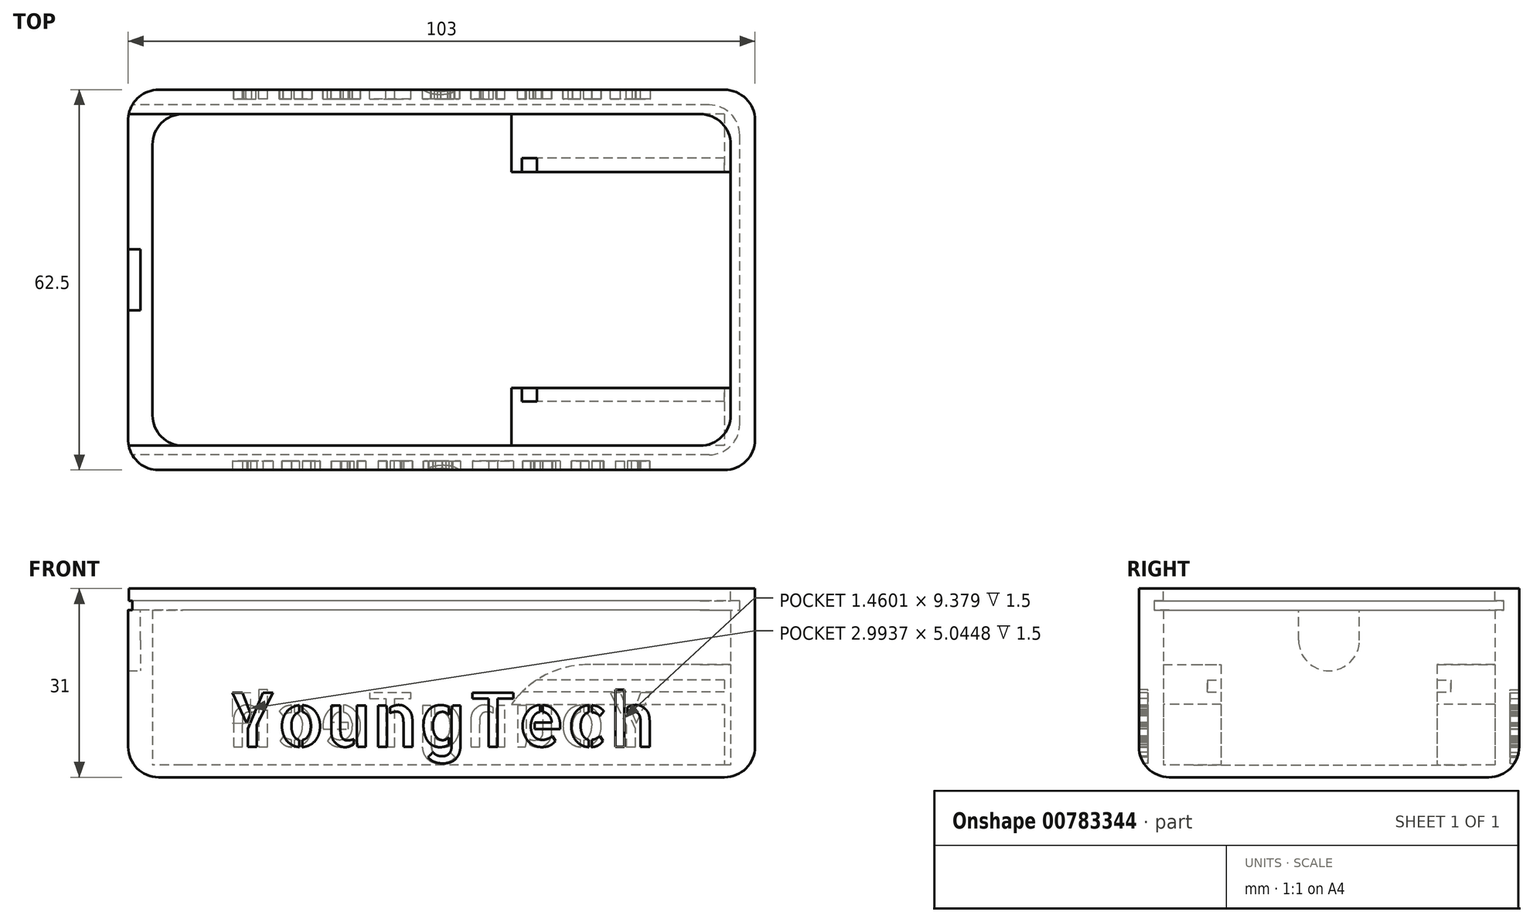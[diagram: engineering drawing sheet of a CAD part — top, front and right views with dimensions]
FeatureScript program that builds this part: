
annotation { "Feature Type Name" : "Feature", "Feature Type Description" : "" }
export const myFeature = defineFeature(function(context is Context, id is Id, definition is map)
    precondition{}
    {
        {
            var Q0;
            Q0=qCreatedBy(makeId("Top.planeOp"),FACE);
            var sketch = newSketch(context, id + "F0", { "sketchPlane" : qUnion([Q0])});
            skLineSegment(sketch, "E0.bottom", {"start": v(51.5, -31.25) * mm, "end": v(-51.5, -31.25) * mm});
            skLineSegment(sketch, "E0.top", {"start": v(51.5, 31.25) * mm, "end": v(-51.5, 31.25) * mm});
            skLineSegment(sketch, "E0.left", {"start": v(51.5, -31.25) * mm, "end": v(51.5, 31.25) * mm});
            skLineSegment(sketch, "E0.right", {"start": v(-51.5, -31.25) * mm, "end": v(-51.5, 31.25) * mm});
            skPoint(sketch, "E0.middle", {"position": v(0, 0) * mm});
            skSolve(sketch);
        }
        {
            var Q0;
            Q0=qSketchRegion(id+"F0",true);
            extrude(context, id + "F1", {"entities" : qUnion([Q0]), "depth" : 2 * mm, "offsetDistance" : 25 * mm});
        }
        {
            var Q0;
            Q0=makeQuery(id+"F1.opExtrude","CAP_FACE",FACE,{"disambiguationData":[OSD([sQuery(id+"F0.wireOp",EDGE,"E0.bottom"),sQuery(id+"F0.wireOp",EDGE,"E0.top"),sQuery(id+"F0.wireOp",EDGE,"E0.left"),sQuery(id+"F0.wireOp",EDGE,"E0.right")])],"isStart":false});
            var sketch = newSketch(context, id + "F2", { "sketchPlane" : qUnion([Q0])});
            skLineSegment(sketch, "E1.0.0", {"start": v(51.5, 31.25) * mm, "end": v(51.5, -31.25) * mm});
            skLineSegment(sketch, "E1.0.1", {"start": v(51.5, -31.25) * mm, "end": v(-51.5, -31.25) * mm});
            skLineSegment(sketch, "E1.0.2", {"start": v(-51.5, -31.25) * mm, "end": v(-51.5, 31.25) * mm});
            skLineSegment(sketch, "E1.0.3", {"start": v(-51.5, 31.25) * mm, "end": v(51.5, 31.25) * mm});
            skLineSegment(sketch, "E2.bottom", {"start": v(47.5, -27.25) * mm, "end": v(-47.5, -27.25) * mm});
            skLineSegment(sketch, "E2.top", {"start": v(47.5, 27.25) * mm, "end": v(-47.5, 27.25) * mm});
            skLineSegment(sketch, "E2.left", {"start": v(47.5, -27.25) * mm, "end": v(47.5, 27.25) * mm});
            skLineSegment(sketch, "E2.right", {"start": v(-47.5, -27.25) * mm, "end": v(-47.5, 27.25) * mm});
            skPoint(sketch, "E2.middle", {"position": v(0, 0) * mm});
            skSolve(sketch);
        }
        {
            var Q0;
            Q0=makeQuery(id+"F2.imprint","IMPRINT",FACE,{"disambiguationData":[TD([[makeQuery(id+"F2.imprint","IMPRINT",EDGE,{"derivedFrom":sQuery(id+"F2.wireOp",EDGE,"E1.0.0")}),1.0]])]});
            extrude(context, id + "F3", {"entities" : qUnion([Q0]), "operationType" : NewBodyOperationType.ADD, "depth" : 29 * mm, "offsetDistance" : 25 * mm});
        }
        {
            var Q0;
            Q0=makeQuery(id+"F3.boolean.opBoolean","MERGE",EDGE,{"derivedFrom":[makeQuery(id+"F1.opExtrude","SWEPT_EDGE",EDGE,{"disambiguationData":[OSD([sQuery(id+"F0.wireOp",EDGE,"E0.top"),sQuery(id+"F0.wireOp",EDGE,"E0.right")])]}),makeQuery(id+"F3.opExtrude","SWEPT_EDGE",EDGE,{"disambiguationData":[OSD([sQuery(id+"F2.wireOp",EDGE,"E1.0.2"),sQuery(id+"F2.wireOp",EDGE,"E1.0.3")])]})]});
            var Q1;
            Q1=makeQuery(id+"F3.boolean.opBoolean","MERGE",EDGE,{"derivedFrom":[makeQuery(id+"F1.opExtrude","SWEPT_EDGE",EDGE,{"disambiguationData":[OSD([sQuery(id+"F0.wireOp",EDGE,"E0.bottom"),sQuery(id+"F0.wireOp",EDGE,"E0.right")])]}),makeQuery(id+"F3.opExtrude","SWEPT_EDGE",EDGE,{"disambiguationData":[OSD([sQuery(id+"F2.wireOp",EDGE,"E1.0.1"),sQuery(id+"F2.wireOp",EDGE,"E1.0.2")])]})]});
            var Q2;
            Q2=makeQuery(id+"F3.boolean.opBoolean","MERGE",EDGE,{"derivedFrom":[makeQuery(id+"F1.opExtrude","SWEPT_EDGE",EDGE,{"disambiguationData":[OSD([sQuery(id+"F0.wireOp",EDGE,"E0.bottom"),sQuery(id+"F0.wireOp",EDGE,"E0.left")])]}),makeQuery(id+"F3.opExtrude","SWEPT_EDGE",EDGE,{"disambiguationData":[OSD([sQuery(id+"F2.wireOp",EDGE,"E1.0.0"),sQuery(id+"F2.wireOp",EDGE,"E1.0.1")])]})]});
            var Q3;
            Q3=makeQuery(id+"F3.opExtrude","SWEPT_EDGE",EDGE,{"disambiguationData":[OSD([sQuery(id+"F2.wireOp",EDGE,"E2.top"),sQuery(id+"F2.wireOp",EDGE,"E2.left")])]});
            var Q4;
            Q4=makeQuery(id+"F3.boolean.opBoolean","MERGE",EDGE,{"derivedFrom":[makeQuery(id+"F1.opExtrude","SWEPT_EDGE",EDGE,{"disambiguationData":[OSD([sQuery(id+"F0.wireOp",EDGE,"E0.top"),sQuery(id+"F0.wireOp",EDGE,"E0.left")])]}),makeQuery(id+"F3.opExtrude","SWEPT_EDGE",EDGE,{"disambiguationData":[OSD([sQuery(id+"F2.wireOp",EDGE,"E1.0.0"),sQuery(id+"F2.wireOp",EDGE,"E1.0.3")])]})]});
            var Q5;
            Q5=makeQuery(id+"F3.opExtrude","SWEPT_EDGE",EDGE,{"disambiguationData":[OSD([sQuery(id+"F2.wireOp",EDGE,"E2.top"),sQuery(id+"F2.wireOp",EDGE,"E2.right")])]});
            var Q6;
            Q6=makeQuery(id+"F3.opExtrude","SWEPT_EDGE",EDGE,{"disambiguationData":[OSD([sQuery(id+"F2.wireOp",EDGE,"E2.bottom"),sQuery(id+"F2.wireOp",EDGE,"E2.right")])]});
            var Q7;
            Q7=makeQuery(id+"F3.opExtrude","SWEPT_EDGE",EDGE,{"disambiguationData":[OSD([sQuery(id+"F2.wireOp",EDGE,"E2.bottom"),sQuery(id+"F2.wireOp",EDGE,"E2.left")])]});
            fillet(context, id + "F4", {"entities" : qUnion([Q0, Q1, Q2, Q3, Q4, Q5, Q6, Q7]), "radius" : 5 * mm, "tangentPropagation" : true, "allowEdgeOverflow" : false});
        }
        {
            var Q0;
            Q0=makeQuery(id+"F3.boolean.opBoolean","MERGE",FACE,{"derivedFrom":[makeQuery(id+"F1.opExtrude","SWEPT_FACE",FACE,{"disambiguationData":[OSD([sQuery(id+"F0.wireOp",EDGE,"E0.right")])]}),makeQuery(id+"F3.opExtrude","SWEPT_FACE",FACE,{"disambiguationData":[OSD([sQuery(id+"F2.wireOp",EDGE,"E1.0.2")])]})]});
            var sketch = newSketch(context, id + "F5", { "sketchPlane" : qUnion([Q0])});
            skLineSegment(sketch, "E3.top", {"start": v(27.25, 31) * mm, "end": v(-27.25, 31) * mm});
            skLineSegment(sketch, "E3.left", {"start": v(27.25, 29) * mm, "end": v(27.25, 31) * mm});
            skLineSegment(sketch, "E3.right", {"start": v(-27.25, 29) * mm, "end": v(-27.25, 31) * mm});
            skLineSegment(sketch, "E4.bottom", {"start": v(28.75, 27.5) * mm, "end": v(-28.75, 27.5) * mm});
            skLineSegment(sketch, "E4.top", {"start": v(28.75, 29) * mm, "end": v(27.25, 29) * mm});
            skLineSegment(sketch, "E4.left", {"start": v(28.75, 27.5) * mm, "end": v(28.75, 29) * mm});
            skLineSegment(sketch, "E4.right", {"start": v(-28.75, 27.5) * mm, "end": v(-28.75, 29) * mm});
            skLineSegment(sketch, "E5.trimOffspring", {"start": v(-27.25, 29) * mm, "end": v(-28.75, 29) * mm});
            skLineSegment(sketch, "E6", {"start": v(0, 31) * mm, "end": v(0, 58.06) * mm, "construction": true});
            skSolve(sketch);
        }
        {
            var Q0;
            Q0=qSketchRegion(id+"F5",true);
            extrude(context, id + "F6", {"entities" : qUnion([Q0]), "operationType" : NewBodyOperationType.REMOVE, "oppositeDirection" : true, "depth" : 99 * mm, "offsetDistance" : 25 * mm});
        }
        {
            var Q0;
            Q0=makeQuery(id+"F6.boolean.opBoolean","COPY",FACE,{"derivedFrom":makeQuery(id+"F6.opExtrude","SWEPT_FACE",FACE,{"disambiguationData":[OSD([sQuery(id+"F5.wireOp",EDGE,"E4.bottom")])]})});
            var sketch = newSketch(context, id + "F7", { "sketchPlane" : qUnion([Q0])});
            skLineSegment(sketch, "E7", {"start": v(0, 0) * mm, "end": v(-47.5, 0) * mm, "construction": true});
            skLineSegment(sketch, "E8.bottom", {"start": v(-32.5, 2.5) * mm, "end": v(-33.5, 2.5) * mm});
            skLineSegment(sketch, "E8.top", {"start": v(-32.5, -2.5) * mm, "end": v(-33.5, -2.5) * mm});
            skLineSegment(sketch, "E8.left", {"start": v(-32.5, 2.5) * mm, "end": v(-32.5, -2.5) * mm});
            skLineSegment(sketch, "E8.right", {"start": v(-33.5, 2.5) * mm, "end": v(-33.5, -2.5) * mm});
            skSolve(sketch);
        }
        {
            var Q0;
            Q0=qSketchRegion(id+"F7",true);
            extrude(context, id + "F8", {"entities" : qUnion([Q0]), "operationType" : NewBodyOperationType.REMOVE, "oppositeDirection" : true, "depth" : 5 * mm, "offsetDistance" : 25 * mm});
        }
        {
            var Q0;
            Q0=makeQuery(id+"F6.boolean.opBoolean","COPY",EDGE,{"derivedFrom":makeQuery(id+"F6.opExtrude","CAP_EDGE",EDGE,{"disambiguationData":[OSD([sQuery(id+"F5.wireOp",EDGE,"E3.left")])],"isStart":false})});
            var Q1;
            Q1=makeQuery(id+"F6.boolean.opBoolean","COPY",EDGE,{"derivedFrom":makeQuery(id+"F6.opExtrude","CAP_EDGE",EDGE,{"disambiguationData":[OSD([sQuery(id+"F5.wireOp",EDGE,"E3.right")])],"isStart":false})});
            fillet(context, id + "F9", {"entities" : qUnion([Q0, Q1]), "radius" : 5 * mm, "tangentPropagation" : true, "allowEdgeOverflow" : false});
        }
        {
            var Q0;
            Q0=makeQuery(id+"F6.boolean.opBoolean","MERGE",FACE,{"derivedFrom":[makeQuery(id+"F3.opExtrude","SWEPT_FACE",FACE,{"disambiguationData":[OSD([sQuery(id+"F2.wireOp",EDGE,"E2.left")])]}),makeQuery(id+"F6.opExtrude","CAP_FACE",FACE,{"disambiguationData":[OSD([sQuery(id+"F5.wireOp",EDGE,"E3.top"),sQuery(id+"F5.wireOp",EDGE,"E3.left"),sQuery(id+"F5.wireOp",EDGE,"E3.right"),sQuery(id+"F5.wireOp",EDGE,"E4.bottom"),sQuery(id+"F5.wireOp",EDGE,"E4.top"),sQuery(id+"F5.wireOp",EDGE,"E4.left"),sQuery(id+"F5.wireOp",EDGE,"E4.right"),sQuery(id+"F5.wireOp",EDGE,"E5.trimOffspring")])],"isStart":false})]});
            var sketch = newSketch(context, id + "F10", { "sketchPlane" : qUnion([Q0])});
            skLineSegment(sketch, "E9.0.2", {"start": v(28.75, 29) * mm, "end": v(-28.75, 29) * mm});
            skLineSegment(sketch, "E9.0.3", {"start": v(-28.75, 29) * mm, "end": v(-28.75, 27.5) * mm});
            skLineSegment(sketch, "E9.0.4", {"start": v(-28.75, 27.5) * mm, "end": v(28.75, 27.5) * mm});
            skLineSegment(sketch, "E9.0.9", {"start": v(28.75, 27.5) * mm, "end": v(28.75, 29) * mm});
            skPoint(sketch, "E10.orphan", {"position": v(-22.25, 29) * mm});
            skPoint(sketch, "E11.orphan", {"position": v(-22.25, 27.5) * mm});
            skSolve(sketch);
        }
        {
            var Q0;
            Q0=qSketchRegion(id+"F10",true);
            extrude(context, id + "F11", {"entities" : qUnion([Q0]), "operationType" : NewBodyOperationType.REMOVE, "oppositeDirection" : true, "depth" : 1.5 * mm, "offsetDistance" : 25 * mm});
        }
        {
            var Q0;
            Q0=makeQuery(id+"F11.boolean.opBoolean","COPY",EDGE,{"derivedFrom":makeQuery(id+"F11.opExtrude","CAP_EDGE",EDGE,{"disambiguationData":[OSD([sQuery(id+"F10.wireOp",EDGE,"E9.0.9")])],"isStart":false})});
            var Q1;
            Q1=makeQuery(id+"F11.boolean.opBoolean","COPY",EDGE,{"derivedFrom":makeQuery(id+"F11.opExtrude","CAP_EDGE",EDGE,{"disambiguationData":[OSD([sQuery(id+"F10.wireOp",EDGE,"E9.0.3")])],"isStart":false})});
            fillet(context, id + "F12", {"entities" : qUnion([Q0, Q1]), "radius" : 5 * mm, "tangentPropagation" : true, "allowEdgeOverflow" : false});
        }
        {
            var Q0;
            Q0=makeQuery(id+"F3.boolean.opBoolean","MERGE",FACE,{"derivedFrom":[makeQuery(id+"F1.opExtrude","SWEPT_FACE",FACE,{"disambiguationData":[OSD([sQuery(id+"F0.wireOp",EDGE,"E0.top")])]}),makeQuery(id+"F3.opExtrude","SWEPT_FACE",FACE,{"disambiguationData":[OSD([sQuery(id+"F2.wireOp",EDGE,"E1.0.3")])]})]});
            var sketch = newSketch(context, id + "F13", { "sketchPlane" : qUnion([Q0])});
            skText(sketch, "E12", { "text": "YoungTech", "fontName": "AllertaStencil-Regular.ttf"});
            skLineSegment(sketch, "E13", {"start": v(-46.5, 0) * mm, "end": v(46.5, 31) * mm, "construction": true});
            skLineSegment(sketch, "E14", {"start": v(-46.5, 15.5) * mm, "end": v(46.5, 15.5) * mm, "construction": true});
            const initialGuessF13  = {"E12": [-0.035, 0.005, 1, 0, 0.0089]};
            skSetInitialGuess(sketch, initialGuessF13);
            skSolve(sketch);
        }
        {
            var Q0;
            Q0=qSketchRegion(id+"F13",true);
            extrude(context, id + "F14", {"entities" : qUnion([Q0]), "operationType" : NewBodyOperationType.REMOVE, "oppositeDirection" : true, "depth" : 1.5 * mm, "offsetDistance" : 25 * mm});
        }
        {
            var Q0;
            Q0=makeQuery(id+"F3.boolean.opBoolean","MERGE",FACE,{"derivedFrom":[makeQuery(id+"F1.opExtrude","SWEPT_FACE",FACE,{"disambiguationData":[OSD([sQuery(id+"F0.wireOp",EDGE,"E0.bottom")])]}),makeQuery(id+"F3.opExtrude","SWEPT_FACE",FACE,{"disambiguationData":[OSD([sQuery(id+"F2.wireOp",EDGE,"E1.0.1")])]})]});
            var sketch = newSketch(context, id + "F15", { "sketchPlane" : qUnion([Q0])});
            skText(sketch, "E15", { "text": "YoungTech", "fontName": "AllertaStencil-Regular.ttf"});
            skLineSegment(sketch, "E16", {"start": v(-46.5, 31) * mm, "end": v(46.5, 0) * mm, "construction": true});
            const initialGuessF15  = {"E15": [-0.035, 0.005, 1, 0, 0.0089]};
            skSetInitialGuess(sketch, initialGuessF15);
            skSolve(sketch);
        }
        {
            var Q0;
            Q0=qSketchRegion(id+"F15",true);
            extrude(context, id + "F16", {"entities" : qUnion([Q0]), "operationType" : NewBodyOperationType.REMOVE, "oppositeDirection" : true, "depth" : 1.5 * mm, "offsetDistance" : 25 * mm});
        }
        {
            var Q0;
            Q0=makeQuery(id+"F1.opExtrude","CAP_EDGE",EDGE,{"disambiguationData":[OSD([sQuery(id+"F0.wireOp",EDGE,"E0.bottom")])],"isStart":true});
            fillet(context, id + "F17", {"entities" : qUnion([Q0]), "radius" : 5 * mm, "tangentPropagation" : true, "allowEdgeOverflow" : false});
        }
        {
            var Q0;
            Q0=makeQuery(id+"F3.boolean.opBoolean","MERGE",FACE,{"derivedFrom":[makeQuery(id+"F1.opExtrude","SWEPT_FACE",FACE,{"disambiguationData":[OSD([sQuery(id+"F0.wireOp",EDGE,"E0.right")])]}),makeQuery(id+"F3.opExtrude","SWEPT_FACE",FACE,{"disambiguationData":[OSD([sQuery(id+"F2.wireOp",EDGE,"E1.0.2")])]})]});
            var sketch = newSketch(context, id + "F18", { "sketchPlane" : qUnion([Q0])});
            skLineSegment(sketch, "E17.bottom", {"start": v(5, 17.5) * mm, "end": v(-5, 17.5) * mm});
            skLineSegment(sketch, "E17.top", {"start": v(5, 27.5) * mm, "end": v(-5, 27.5) * mm});
            skLineSegment(sketch, "E17.left", {"start": v(5, 17.5) * mm, "end": v(5, 27.5) * mm});
            skLineSegment(sketch, "E17.right", {"start": v(-5, 17.5) * mm, "end": v(-5, 27.5) * mm});
            skPoint(sketch, "E17.middle", {"position": v(0, 22.5) * mm});
            skSolve(sketch);
        }
        {
            var Q0;
            Q0=qSketchRegion(id+"F18",true);
            extrude(context, id + "F19", {"entities" : qUnion([Q0]), "operationType" : NewBodyOperationType.REMOVE, "oppositeDirection" : true, "depth" : 2 * mm, "offsetDistance" : 25 * mm});
        }
        {
            var Q0;
            Q0=makeQuery(id+"F19.boolean.opBoolean","COPY",EDGE,{"derivedFrom":makeQuery(id+"F19.opExtrude","SWEPT_EDGE",EDGE,{"disambiguationData":[OSD([sQuery(id+"F18.wireOp",EDGE,"E17.bottom"),sQuery(id+"F18.wireOp",EDGE,"E17.right")])]})});
            var Q1;
            Q1=makeQuery(id+"F19.boolean.opBoolean","COPY",EDGE,{"derivedFrom":makeQuery(id+"F19.opExtrude","SWEPT_EDGE",EDGE,{"disambiguationData":[OSD([sQuery(id+"F18.wireOp",EDGE,"E17.bottom"),sQuery(id+"F18.wireOp",EDGE,"E17.left")])]})});
            var Q2;
            Q2=makeQuery(id+"F19.boolean.opBoolean","COPY",EDGE,{"derivedFrom":makeQuery(id+"F19.opExtrude","SWEPT_EDGE",EDGE,{"disambiguationData":[OSD([sQuery(id+"F5.wireOp",EDGE,"E4.bottom"),sQuery(id+"F18.wireOp",EDGE,"E17.top"),sQuery(id+"F18.wireOp",EDGE,"E17.left")])]})});
            var Q3;
            Q3=makeQuery(id+"F19.boolean.opBoolean","COPY",EDGE,{"derivedFrom":makeQuery(id+"F19.opExtrude","SWEPT_EDGE",EDGE,{"disambiguationData":[OSD([sQuery(id+"F5.wireOp",EDGE,"E4.bottom"),sQuery(id+"F18.wireOp",EDGE,"E17.top"),sQuery(id+"F18.wireOp",EDGE,"E17.right")])]})});
            fillet(context, id + "F20", {"entities" : qUnion([Q0, Q1, Q2, Q3]), "radius" : 5 * mm, "tangentPropagation" : true, "allowEdgeOverflow" : false});
        }
        {
            var Q0;
            Q0=makeQuery(id+"F1.opExtrude","CAP_FACE",FACE,{"disambiguationData":[OSD([sQuery(id+"F0.wireOp",EDGE,"E0.bottom"),sQuery(id+"F0.wireOp",EDGE,"E0.top"),sQuery(id+"F0.wireOp",EDGE,"E0.left"),sQuery(id+"F0.wireOp",EDGE,"E0.right")])],"isStart":false});
            var sketch = newSketch(context, id + "F21", { "sketchPlane" : qUnion([Q0])});
            skLineSegment(sketch, "E18", {"start": v(0, 0) * mm, "end": v(65.83, 0) * mm, "construction": true});
            skLineSegment(sketch, "E19.bottom", {"start": v(47.5, 27.25) * mm, "end": v(11.5, 27.25) * mm});
            skLineSegment(sketch, "E19.top", {"start": v(47.5, 17.75) * mm, "end": v(11.5, 17.75) * mm});
            skLineSegment(sketch, "E19.left", {"start": v(47.5, 27.25) * mm, "end": v(47.5, 17.75) * mm});
            skLineSegment(sketch, "E19.right", {"start": v(11.5, 27.25) * mm, "end": v(11.5, 17.75) * mm});
            skLineSegment(sketch, "E20.MirrorCS", {"start": v(47.5, -17.75) * mm, "end": v(11.5, -17.75) * mm});
            skLineSegment(sketch, "E21.MirrorCS", {"start": v(47.5, -27.25) * mm, "end": v(47.5, -17.75) * mm});
            skLineSegment(sketch, "E22.MirrorCS", {"start": v(47.5, -27.25) * mm, "end": v(11.5, -27.25) * mm});
            skLineSegment(sketch, "E23.MirrorCS", {"start": v(11.5, -27.25) * mm, "end": v(11.5, -17.75) * mm});
            skSolve(sketch);
        }
        {
            var Q0;
            {var subQ4=sQuery(id+"F21.wireOp",EDGE,"E19.top");Q0=makeQuery(id+"F21.imprint","IMPRINT",FACE,{"disambiguationData":[TD([[makeQuery(id+"F21.imprint","IMPRINT",EDGE,{"derivedFrom":subQ4}),-1.0]])]});}
            var Q1;
            {var subQ6=sQuery(id+"F21.wireOp",EDGE,"E20.MirrorCS");Q1=makeQuery(id+"F21.imprint","IMPRINT",FACE,{"disambiguationData":[TD([[makeQuery(id+"F21.imprint","IMPRINT",EDGE,{"derivedFrom":subQ6}),1.0]])]});}
            extrude(context, id + "F22", {"entities" : qUnion([Q0, Q1]), "operationType" : NewBodyOperationType.ADD, "depth" : 16.5 * mm, "offsetDistance" : 25 * mm});
        }
        {
            var Q0;
            Q0=makeQuery(id+"F22.opExtrude","SWEPT_FACE",FACE,{"disambiguationData":[OSD([sQuery(id+"F21.wireOp",EDGE,"E19.right")])]});
            var sketch = newSketch(context, id + "F23", { "sketchPlane" : qUnion([Q0])});
            skLineSegment(sketch, "E24.bottom", {"start": v(20, 14) * mm, "end": v(-20, 14) * mm});
            skLineSegment(sketch, "E24.top", {"start": v(20, 16) * mm, "end": v(-20, 16) * mm});
            skLineSegment(sketch, "E24.left", {"start": v(20, 14) * mm, "end": v(20, 16) * mm});
            skLineSegment(sketch, "E24.right", {"start": v(-20, 14) * mm, "end": v(-20, 16) * mm});
            skPoint(sketch, "E24.middle", {"position": v(0, 15) * mm});
            skLineSegment(sketch, "E25", {"start": v(-17.75, 2) * mm, "end": v(0, 2) * mm, "construction": true});
            skLineSegment(sketch, "E26", {"start": v(0, 2) * mm, "end": v(0, 13) * mm, "construction": true});
            skLineSegment(sketch, "E27.bottom", {"start": v(-27.25, 12) * mm, "end": v(27.25, 12) * mm});
            skLineSegment(sketch, "E27.top", {"start": v(-27.25, 2) * mm, "end": v(27.25, 2) * mm});
            skLineSegment(sketch, "E27.left", {"start": v(-27.25, 12) * mm, "end": v(-27.25, 2) * mm});
            skLineSegment(sketch, "E27.right", {"start": v(27.25, 12) * mm, "end": v(27.25, 2) * mm});
            skSolve(sketch);
        }
        {
            var Q0;
            Q0=qSketchRegion(id+"F23",true);
            extrude(context, id + "F24", {"entities" : qUnion([Q0]), "operationType" : NewBodyOperationType.REMOVE, "oppositeDirection" : true, "depth" : 35 * mm, "offsetDistance" : 25 * mm});
        }
        {
            var Q0;
            Q0=makeQuery(id+"F22.opExtrude","CAP_EDGE",EDGE,{"disambiguationData":[OSD([sQuery(id+"F21.wireOp",EDGE,"E19.right")])],"isStart":false});
            var Q1;
            Q1=makeQuery(id+"F22.opExtrude","CAP_EDGE",EDGE,{"disambiguationData":[OSD([sQuery(id+"F21.wireOp",EDGE,"E23.MirrorCS")])],"isStart":false});
            fillet(context, id + "F25", {"entities" : qUnion([Q0, Q1]), "radius" : 15.5 * mm, "tangentPropagation" : true, "allowEdgeOverflow" : false});
        }
    });
